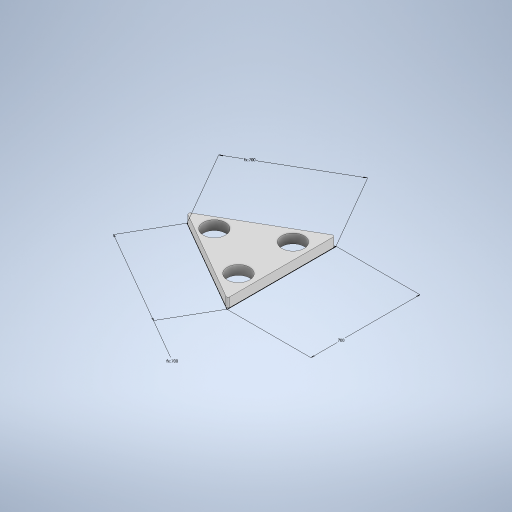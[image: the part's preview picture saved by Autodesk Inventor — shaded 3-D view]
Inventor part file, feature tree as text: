
AUTODESK INVENTOR PART (.ipt)
format: ipt  version: 2023.2 (Build 272271000, 271)  size: 266,240 bytes
history: native  units: mm
features: fillet x3, sketch x1, extrude x1, hole x1
ambient origin geometry x8: Origin, YZ Plane, XZ Plane, XY Plane, X Axis, Y Axis, Z Axis, Center Point
bodies: Solid1 (feature_tree)
feature tree (6):
  sketch  "Sketch1"  dims[d0=700.0mm d1=700.0mm d2=700.0mm d3=60.0mm d4=0.0mm d19=143.0mm d20=6.0mm d21=4.0mm d22=2.0mm d23=90.0deg d24=8.0mm d25=20.594885mm d26=10.0mm d27=10.0mm d28=10.0mm d5=1.0mm d6=1.0mm d7=1.0mm d8=0.15mm d9=0.25mm d10=0.375mm d11=14.3117mm d12=0.75mm d13=20.594885mm d14=0.0625mm d15=0.75mm d16=0.375mm]
  extrude  "Extrusion1"  Depth=700.0mm
  hole  "Hole3"  [1 undecoded]
  fillet  "Fillet1"  Radius=60.0mm
  fillet  "Fillet2"  Radius=10.0mm
  fillet  "Fillet3"  Radius=10.0mm
note: 1 required parameter value undecoded (feature->parameter linkage not recoverable at this tier; creation-order binding heuristic only, values carry confidence <= 0.55)
